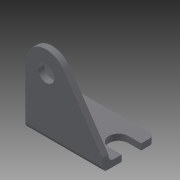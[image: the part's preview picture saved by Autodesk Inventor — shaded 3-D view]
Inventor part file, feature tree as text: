
AUTODESK INVENTOR PART (.ipt)
format: ipt  version: 2014 (Build 180170000, 170)  size: 158,208 bytes
history: native  units: in
note: dims shown in document units (in); Inventor stores cm internally (conversion verified against a paired STEP export)
features: other x28, sketch x8, extrude x5, hole x3
ambient origin geometry x8: Origin, YZ Plane, XZ Plane, XY Plane, X Axis, Y Axis, Z Axis, Center Point
bodies: Solid1 (feature_tree)
feature tree (44):
  extrude  "Extrusion1"  Depth=0.51in TaperAngle=0.0deg
  extrude  "Extrusion2"  Depth=0.0598in TaperAngle=0.0deg
  hole  "Hole1"  [1 undecoded]
  hole  "Hole2"  [1 undecoded]
  hole  "Hole3"  [1 undecoded]
  sketch  "Sketch_6"
  sketch  "Sketch_7"
  extrude  "Extrusion3"  [1 undecoded]
  extrude  "Extrusion4"  [1 undecoded]
  extrude  "Extrusion5"  [1 undecoded]
  other  "c2_XY"
  other  "c2_YZ"
  other  "c2_ZX"
  other  "c2_X"
  other  "c2_Y"
  other  "c2_Z"
  other  "c2_Center"
  other  "k2_XY"
  other  "k2_YZ"
  other  "k2_ZX"
  other  "k2_X"
  other  "k2_Y"
  other  "k2_Z"
  other  "k2_Center"
  other  "to_dummy_R_XY"
  other  "to_dummy_R_YZ"
  other  "to_dummy_R_ZX"
  other  "to_dummy_R_X"
  other  "to_dummy_R_Y"
  other  "to_dummy_R_Z"
  other  "to_dummy_R_Center"
  other  "to_pin_R_XY"
  other  "to_pin_R_YZ"
  other  "to_pin_R_ZX"
  other  "to_pin_R_X"
  other  "to_pin_R_Y"
  other  "to_pin_R_Z"
  other  "to_pin_R_Center"
  sketch  "Sketch_1"  dims[d0=0.75in d1=0.0in d2=0.51in d3=0.0in]
  sketch  "Sketch_2"  dims[d4=0.1585in d5=0.75in d6=0.375in d7=0.25in d8=0.5635in d9=0.0598in d10=0.0in]
  sketch  "Sketch3"  dims[d11=0.19in d12=0.75in d13=0.375in d14=0.25in d15=0.5635in d16=0.0598in d17=0.0in]
  sketch  "Sketch4"  dims[d18=0.19in d19=0.75in d20=0.375in d21=0.25in d22=0.5635in d23=0.0598in d24=0.0in d25=0.0598in d26=0.0in]
  sketch  "Sketch5"  dims[d27=0.0598in d28=0.0in d29=0.0598in d30=0.0in]
  sketch  "Sketch_8"
note: 6 required parameter values undecoded (feature->parameter linkage not recoverable at this tier; creation-order binding heuristic only, values carry confidence <= 0.55)
